# Revit family: VT.382.B.06
name_source: partatom
category: Оборудование
units: mm (PartAtom-declared; Revit-internal decimal feet)

## family parameters
Всегда вертикально = Да
Заголовок OmniClass = Climate Control (HVAC)
На основе рабочей плоскости = Нет
Номер OmniClass = 23.75.00.00
Общий = Нет
При загрузке вырезать с полостями = Нет
Размер круглого соединителя = Использовать диаметр
Тип детали = Нормальный
Точка расчета площади = Нет

## types (1)
- VT.382.B.06
    BIMobject категория = Другой
    BIMobject код категории = ОВК-другой
    BIMobject код основной категории = ОВК
    BIMobject основная категория = HVAC
    EMCS Version = 3.0
    IFC классификация = Клапан
    Revit Version = 2018
    URL = https://valtec.ru
    Uniclass 1.4 Описани = Водопроводные системы
    Uniclass 2.0 Описани = Фильтры для воды и фильтр
    Uniclass 2015 Имя = Фильтры для воды
    Uniformat II Описание = HVAC
    Вес нетто (Kg) = 0
    Группа модели = DIRTSTOP® XL
    Данные продукта url = https://bimobject.com
    Жидкость для нанесения = Вода и гликолевые растворы
    Изготовитель = IVAR
    Инструкции по установке = https://valtec.ru
    Макс рабочая температура = 90 °C
    Макс рабочее давление = 3 bar
    Максимальный процент гликоля (%) = 50
    Максимальный расход (m3/h) = 2.1 м³/ч
    Марка url = https://valtec.ru
    Мастерформат 2014 Описание = Отопление, вентиляция и кондиционирование воздуха (HVAC)
    Материал = PA66 + GF 30%
    Материал вторичный = Латунь
    Материал основной = Полиамид
    Минимальная рабочая температура = 0 °C
    Название производителя = IVAR
    Номинальная высота = 0 мм
    Номинальная ширина = 0 мм
    Описание = Высокопроизводительный магнитный сепаратор грязи с тройным фильтрующим действием с магнитом, сетчатым фильтром и циклоническим движением воды
    Описание NBS = Фильтры для воды и фильтр
    Описание OmniClass = Жидкие фильтр
    Описание Конфигурации = Высокопроизводительный магнитный сепаратор грязи с тройным фильтрующим действием с магнитом, сетчатым фильтром и циклоническим движением воды.
    Описание статьи = Высокопроизводительный магнитный сепаратор грязи с тройным фильтрующим действием с магнитом, сетчатым фильтром и циклоническим движением воды
    Практическое руководство по использованию семьи = - Вы должны выбрать диаметр соединения. Доступные соединения: ø22F, ¾ ”F (DN20), 1” F (DN25), 1 ”1 / 4F (DN32). Смотрите эту опцию в параметре «Размеры - DN».
- Вы должны выбрать угол соединения части. Отметьте эту опцию в параметрах «Свойства модели - вертикальное соединение» или «Свойства модели - горизонтальное соединение» или «Свойства модели - соединение 45 °» или «Свойства модели - соединение 135 °». Внимание! Выберите один и только один угол подключения.
    Продукт url = https://valtec.ru
    Произведено в = Сделано в Италии
    Размер соединения = ø22, 3/4F (DN20), 1F (DN25), 1 1/4F (DN32)
    Рейтинг разделения частиц = 500 µm (first cleaning), 800 µm (standard operation)
    Страна производитель = Italy
    Техническое описание = https://valtec.ru
